# Revit family: 9600-P
name_source: partatom
category: Plumbing Fixtures
units: mm (PartAtom-declared; Revit-internal decimal feet)

## family parameters
Cut with Voids When Loaded = No
Host = Face
OmniClass Number = 23.65.70.11.11
OmniClass Title = Fixtures for Liquids
Part Type = Normal
Room Calculation Point = No
Round Connector Dimension = Use Diameter
Shared = No

## types (4) — shared parameters
Model = Not Available
Product Material = Chrome - Symmons - Polished
z Error = No
z GPM GPM = 0.000 GPM
z Has Rebuild Kit Trim Only = No
z Has Trim = No
zero-valued in all types: Default Elevation, z GPM Number, z Type, z Type Finish, z Type GPM

## per-type parameters (varying)
| type | Gallons Per Minute |
| 1.2 GPM Flow Restrictor, Chrome | 1.200 GPM |
| 1.5 GPM Flow Restrictor, Chrome | 1.500 GPM |
| 1.75 GPM Flow Restrictor, Chrome | 1.750 GPM |
| 2 GPM Flow Restrictor, Chrome | 2.000 GPM |

## geometry (parser evidence)
native form markers: Blend x2, Sweep x7
no freeform markers — native parametric forms only
